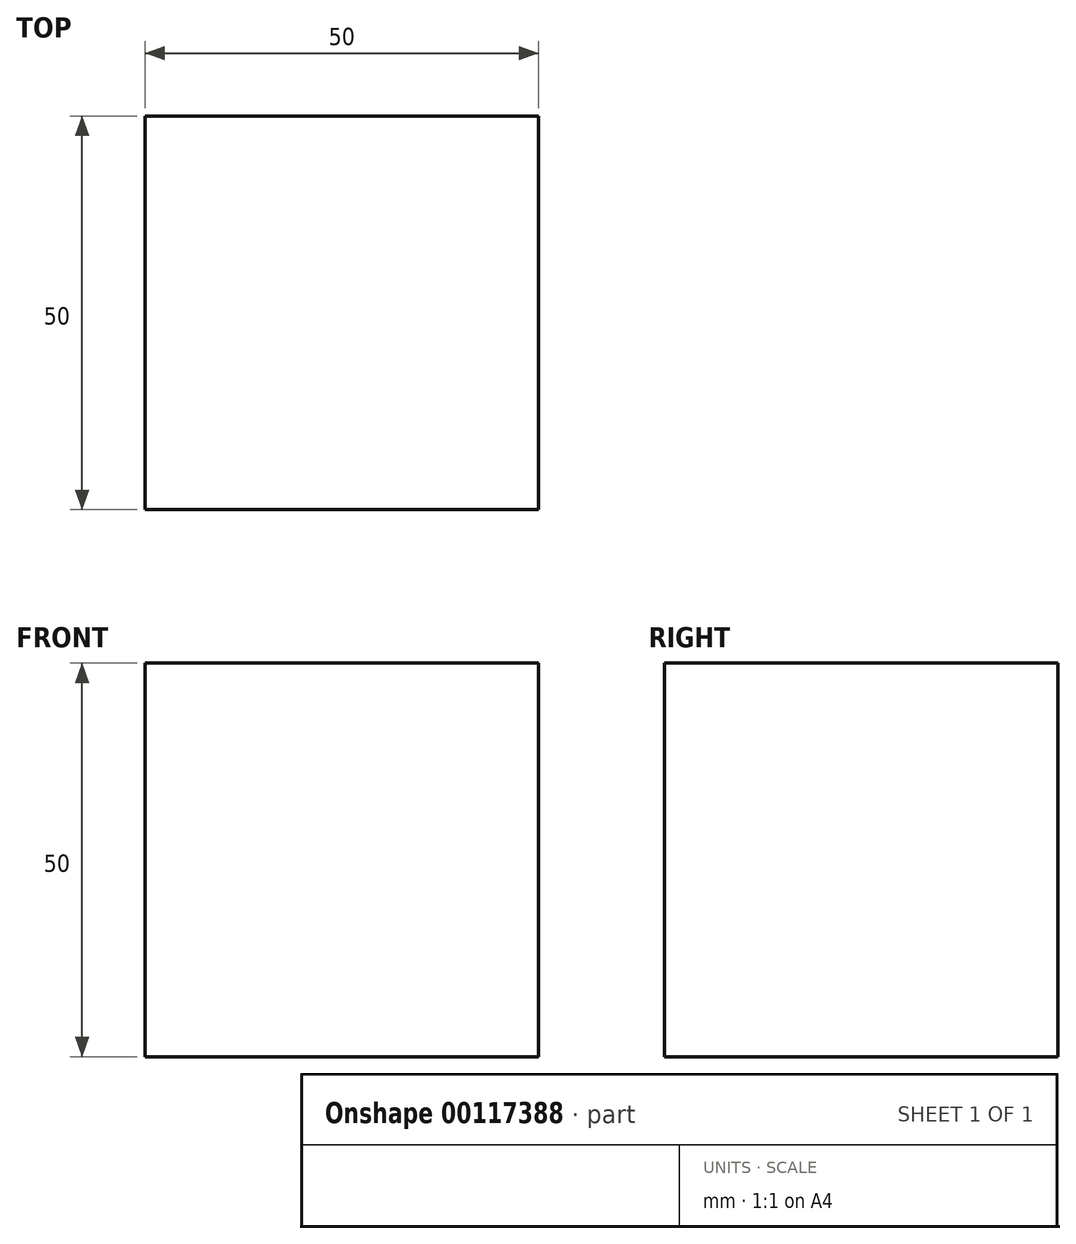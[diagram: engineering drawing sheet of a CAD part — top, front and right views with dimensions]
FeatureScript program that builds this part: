
annotation { "Feature Type Name" : "Feature", "Feature Type Description" : "" }
export const myFeature = defineFeature(function(context is Context, id is Id, definition is map)
    precondition{}
    {
        {
            var Q0;
            Q0=qCreatedBy(makeId("Top.planeOp"),FACE);
            var sketch = newSketch(context, id + "F0", { "sketchPlane" : qUnion([Q0])});
            skLineSegment(sketch, "E0.bottom", {"start": v(28.97, -24.94) * mm, "end": v(-21.03, -24.94) * mm});
            skLineSegment(sketch, "E0.top", {"start": v(28.97, 25.06) * mm, "end": v(-21.03, 25.06) * mm});
            skLineSegment(sketch, "E0.left", {"start": v(28.97, -24.94) * mm, "end": v(28.97, 25.06) * mm});
            skLineSegment(sketch, "E0.right", {"start": v(-21.03, -24.94) * mm, "end": v(-21.03, 25.06) * mm});
            skPoint(sketch, "E0.middle", {"position": v(3.97, 0.06) * mm});
            skSolve(sketch);
        }
        {
            var Q0;
            Q0 = qSketchRegion(id + "F0", true);
            extrude(context, id + "F1", {"entities" : qUnion([Q0]), "depth" : 50 * mm, "symmetric" : true});
        }
    });
